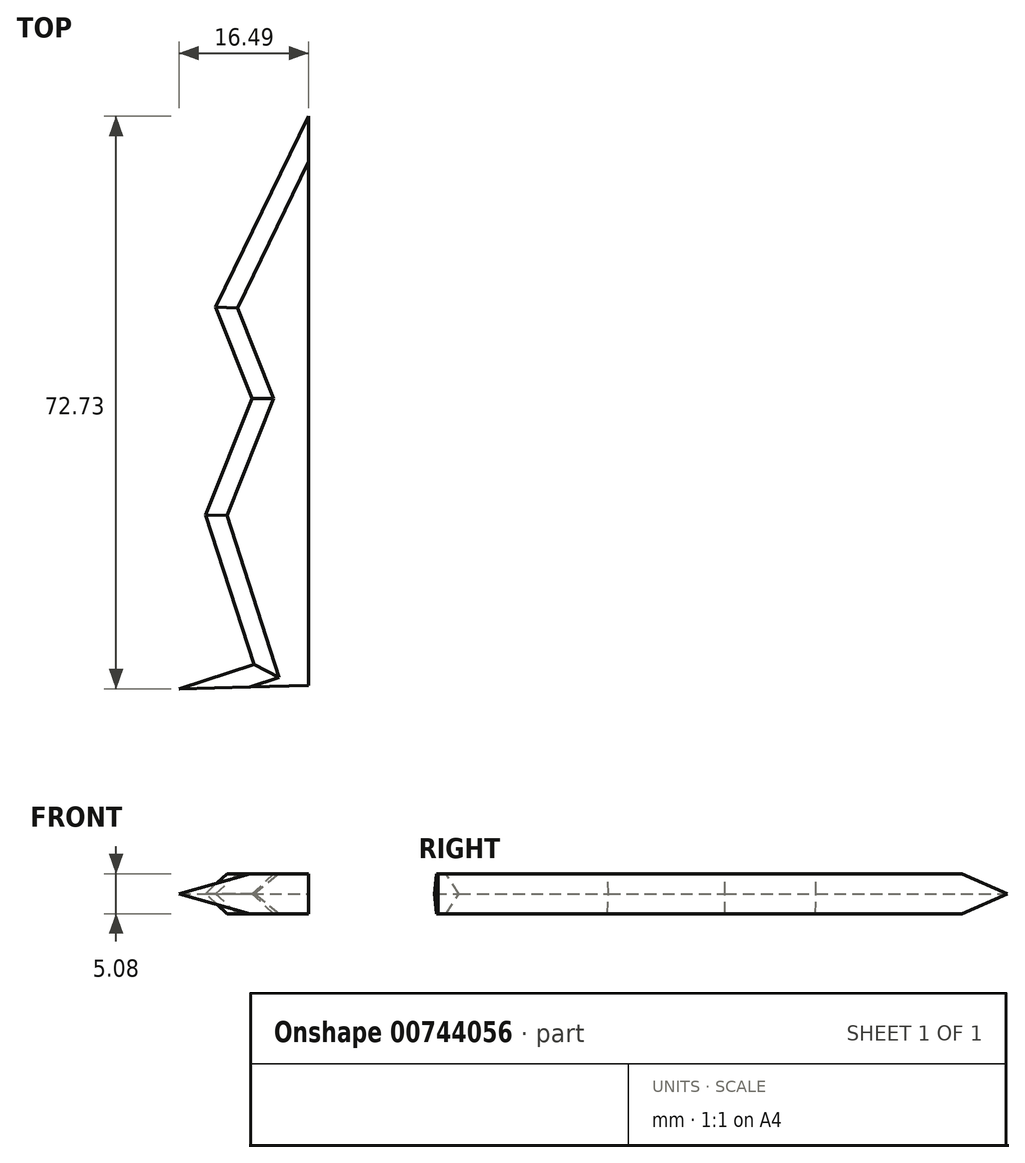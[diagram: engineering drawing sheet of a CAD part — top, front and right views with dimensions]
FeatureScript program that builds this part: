
annotation { "Feature Type Name" : "Feature", "Feature Type Description" : "" }
export const myFeature = defineFeature(function(context is Context, id is Id, definition is map)
    precondition{}
    {
        {
            var Q0;
            Q0=qCreatedBy(makeId("Top.planeOp"),FACE);
            var sketch = newSketch(context, id + "F0", { "sketchPlane" : qUnion([Q0])});
            skLineSegment(sketch, "E0", {"start": v(0, 72.3) * mm, "end": v(-11.83, 48.03) * mm});
            skLineSegment(sketch, "E1", {"start": v(-11.83, 48.03) * mm, "end": v(-7.19, 36.42) * mm});
            skLineSegment(sketch, "E2", {"start": v(-7.19, 36.42) * mm, "end": v(-13.1, 21.64) * mm});
            skLineSegment(sketch, "E3", {"start": v(-13.1, 21.64) * mm, "end": v(-6.98, 2.64) * mm});
            skLineSegment(sketch, "E4", {"start": v(-6.98, 2.64) * mm, "end": v(-16.5, -0.43) * mm});
            skLineSegment(sketch, "E5", {"start": v(-16.5, -0.43) * mm, "end": v(0, 0) * mm});
            skLineSegment(sketch, "E6", {"start": v(0, 0) * mm, "end": v(0, 72.3) * mm});
            skSolve(sketch);
        }
        {
            var Q0;
            Q0=makeQuery(id+"F0.imprint","IMPRINT",FACE,{"disambiguationData":[TD([[makeQuery(id+"F0.imprint","IMPRINT",EDGE,{"derivedFrom":sQuery(id+"F0.wireOp",EDGE,"E0")}),1.0]])]});
            extrude(context, id + "F1", {"entities" : qUnion([Q0]), "depth" : 5.08 * mm, "offsetDistance" : 25.4 * mm});
        }
        {
            var Q0;
            Q0=makeQuery(id+"F1.opExtrude","CAP_EDGE",EDGE,{"disambiguationData":[OSD([sQuery(id+"F0.wireOp",EDGE,"E0")])],"isStart":false});
            var Q1;
            Q1=makeQuery(id+"F1.opExtrude","CAP_EDGE",EDGE,{"disambiguationData":[OSD([sQuery(id+"F0.wireOp",EDGE,"E1")])],"isStart":false});
            var Q2;
            Q2=makeQuery(id+"F1.opExtrude","CAP_EDGE",EDGE,{"disambiguationData":[OSD([sQuery(id+"F0.wireOp",EDGE,"E2")])],"isStart":false});
            var Q3;
            Q3=makeQuery(id+"F1.opExtrude","CAP_EDGE",EDGE,{"disambiguationData":[OSD([sQuery(id+"F0.wireOp",EDGE,"E3")])],"isStart":false});
            var Q4;
            Q4=makeQuery(id+"F1.opExtrude","CAP_EDGE",EDGE,{"disambiguationData":[OSD([sQuery(id+"F0.wireOp",EDGE,"E4")])],"isStart":false});
            var Q5;
            Q5=makeQuery(id+"F1.opExtrude","CAP_EDGE",EDGE,{"disambiguationData":[OSD([sQuery(id+"F0.wireOp",EDGE,"E0")])],"isStart":true});
            var Q6;
            Q6=makeQuery(id+"F1.opExtrude","CAP_EDGE",EDGE,{"disambiguationData":[OSD([sQuery(id+"F0.wireOp",EDGE,"E1")])],"isStart":true});
            var Q7;
            Q7=makeQuery(id+"F1.opExtrude","CAP_EDGE",EDGE,{"disambiguationData":[OSD([sQuery(id+"F0.wireOp",EDGE,"E2")])],"isStart":true});
            var Q8;
            Q8=makeQuery(id+"F1.opExtrude","CAP_EDGE",EDGE,{"disambiguationData":[OSD([sQuery(id+"F0.wireOp",EDGE,"E3")])],"isStart":true});
            var Q9;
            Q9=makeQuery(id+"F1.opExtrude","CAP_EDGE",EDGE,{"disambiguationData":[OSD([sQuery(id+"F0.wireOp",EDGE,"E4")])],"isStart":true});
            chamfer(context, id + "F2", {"entities" : qUnion([Q0, Q1, Q2, Q3, Q4, Q5, Q6, Q7, Q8, Q9]), "width" : 2.54 * mm, "tangentPropagation" : true});
        }
    });
